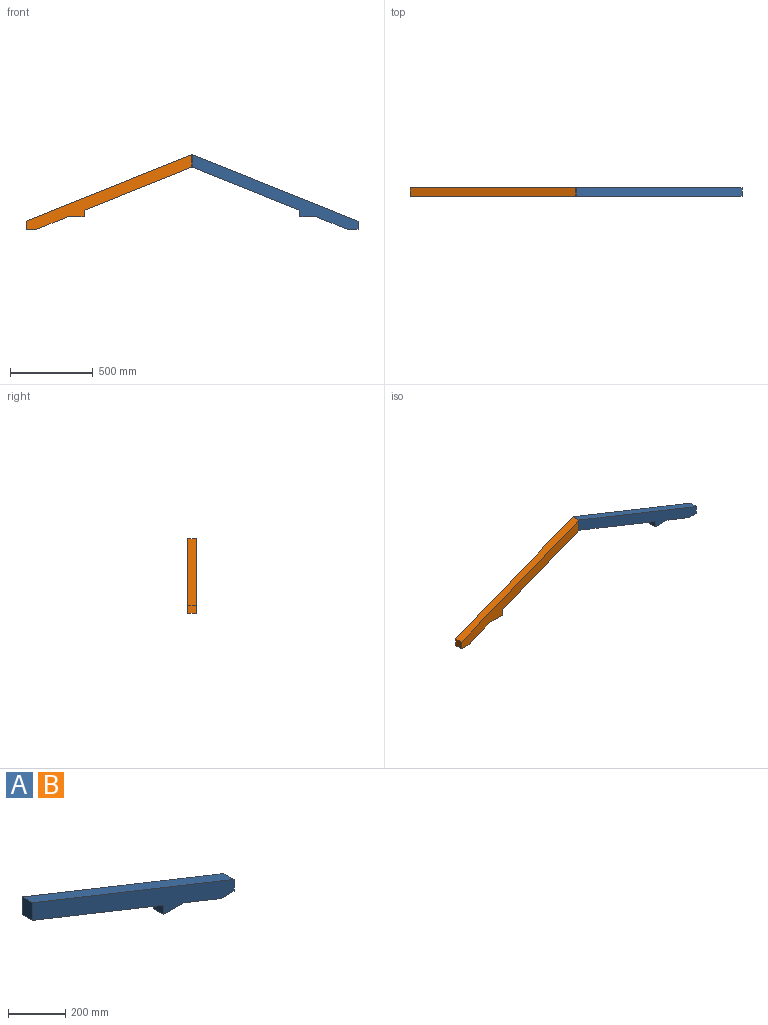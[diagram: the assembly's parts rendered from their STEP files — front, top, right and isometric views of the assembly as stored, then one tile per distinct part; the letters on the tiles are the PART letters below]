
ASSEMBLY  parts=2 mates=1
PART A: 10 faces, bbox 1000x50x450 mm
  f0: plane 1000x400mm, normal (0.37,0,0.93), area 53851.6mm2, adj f1,f7,f8,f9
  f1: plane 75.39x50mm, normal (-1,0,0), area 3769.6mm2, adj f0,f2,f8,f9
  f2: plane 650x260mm, normal (-0.37,0,-0.93), area 35003.6mm2, adj f1,f3,f8,f9
  f3: plane 50x40mm, normal (-1,0,0), area 2000mm2, adj f2,f4,f8,f9
  f4: plane 100x50mm, normal (0,0,-1), area 5000mm2, adj f3,f5,f8,f9
  f5: plane 186.52x74.61mm, normal (-0.37,0,-0.93), area 10044.4mm2, adj f4,f6,f8,f9
  f6: plane 63.48x50mm, normal (0,0,-1), area 3174mm2, adj f5,f7,f8,f9
  f7: plane 50x50mm, normal (1,0,0), area 2500mm2, adj f0,f6,f8,f9
  f8: plane 1000x450mm, normal (0,-1,0), area 76586.3mm2, adj f0,f1,f2,f3,f4,f5,f6,f7
  f9: plane 1000x450mm, normal (0,1,0), area 76586.3mm2, adj f0,f1,f2,f3,f4,f5,f6,f7
PART B: same geometry as A
PLACE A t=(-127.67,170.43,-70.51)mm
PLACE B rot(axis=(0,0,1),180deg) t=(-716.59,120.43,-70.51)mm
MATE fastened B.f1 <-> A.f1  axis (1,0,0) through (-422.13,145.43,138.55)mm
